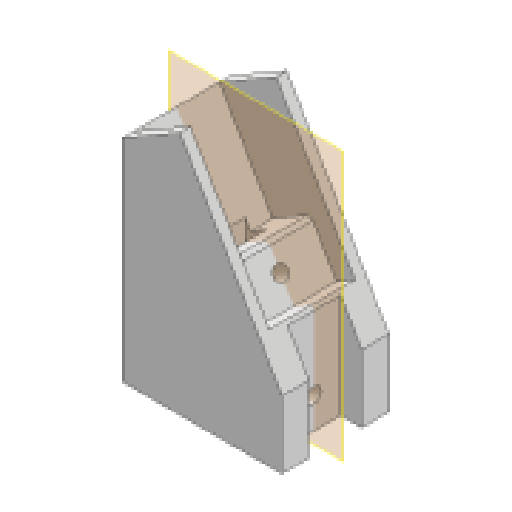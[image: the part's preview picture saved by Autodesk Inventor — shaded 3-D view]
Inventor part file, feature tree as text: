
AUTODESK INVENTOR PART (.ipt)
format: ipt  version: 2025.1 (Build 291241020, 241B)  size: 175,616 bytes
history: native  units: in
note: dims shown in document units (in); Inventor stores cm internally (conversion verified against a paired STEP export)
features: extrude x9, sketch x9, other x7, reference x4, plane x2, mirror x1, chamfer x1, projected_geometry x1
ambient origin geometry x8: Origin, YZ Plane, XZ Plane, XY Plane, X Axis, Y Axis, Z Axis, Center Point
bodies: Solid1 (feature_tree)
feature tree (34):
  extrude  "Extrusion1"  Depth=1.0in
  extrude  "Extrusion2"  Depth=2.0in
  plane  "Work Plane1"
  mirror  "Mirror1"
  extrude  "Extrusion3"  Depth=0.81in TaperAngle=0.0deg
  extrude  "Extrusion4"  Depth=0.5in
  plane  "Work Plane2"
  extrude  "Extrusion5"  Depth=0.25in
  extrude  "Extrusion6"  Depth=0.6in TaperAngle=0.0deg
  chamfer  "Chamfer1"  Distance=0.4in
  extrude  "Extrusion7"  Depth=0.2in TaperAngle=0.0deg
  extrude  "Extrusion8"  Depth=0.6in
  extrude  "Extrusion9"  Depth=0.3in TaperAngle=0.0deg
  sketch  "Sketch1"  dims[d0=0.618in d1=1.0in]
  sketch  "Sketch2"  dims[d2=1.5in d3=2.0in]
  projected_geometry  "Projected Loop1"
  sketch  "Sketch3"  dims[d4=120.0deg d5=0.81in d6=0.0in]
  sketch  "Sketch4"  dims[d7=0.1in d8=0.0in d9=0.5in]
  reference  "Reference1"
  sketch  "Sketch5"  dims[d10=0.2in d11=0.25in]
  sketch  "Sketch6"  dims[d12=1.3375in d13=0.0in d14=0.6in d15=0.0in]
  sketch  "Sketch7"  dims[d16=0.2in d17=0.4in d18=0.0in]
  sketch  "Sketch8"  dims[d19=0.487in d20=0.2in d21=0.0in]
  reference  "Reference2"
  sketch  "Sketch9"  dims[d22=0.04in d23=0.125in d24=45.0deg d25=0.14in d26=0.3in d27=0.0in d28=0.6in d29=0.0in d30=0.6in d31=0.0in]
  reference  "Reference3"
  reference  "Reference5"
  parser-record x2  (decoder bookkeeping rows leaked as tree rows — omitted from the tree; the rows remain in map.json)
  other  "Finger Assem.iam"
  other  "KNUCKLE 1:1"
  other  "Hand Assem.iam"
  other  "Palm:1"
  other  "Wrist Base:1"
note: 2 file-system paths scrubbed to <path> (originals preserved in map.json)
